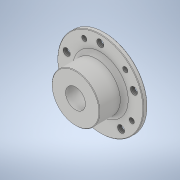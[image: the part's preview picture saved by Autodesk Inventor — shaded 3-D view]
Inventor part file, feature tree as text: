
AUTODESK INVENTOR PART (.ipt)
format: ipt  version: 2021 (Build 250183000, 183)  size: 223,232 bytes
history: native  units: in
note: dims shown in document units (in); Inventor stores cm internally (conversion verified against a paired STEP export)
features: thread x11, sketch x6, extrude x5, fillet x2, revolve x1, chamfer x1
ambient origin geometry x8: Origin, YZ Plane, XZ Plane, XY Plane, X Axis, Y Axis, Z Axis, Center Point
bodies: Solid1 (feature_tree)
feature tree (26):
  revolve  "Revolution1"  [1 undecoded]
  extrude  "Extrusion1"  Depth=0.26in
  extrude  "Extrusion2"  Depth=0.2in
  fillet  "Fillet1"  Radius=0.16in
  chamfer  "Chamfer1"  Distance=1.0in
  fillet  "Fillet2"  Radius=1.25in
  extrude  "Extrusion3"  Depth=0.26in TaperAngle=0.0deg
  thread  "Thread1"  [1 undecoded]
  thread  "Thread2"  [1 undecoded]
  thread  "Thread3"  [1 undecoded]
  thread  "Thread4"  [1 undecoded]
  thread  "Thread5"  [1 undecoded]
  thread  "Thread6"  [1 undecoded]
  extrude  "Extrusion4"  TaperAngle=45.0deg  [1 undecoded]
  extrude  "Extrusion5"  Depth=0.26in
  thread  "Thread7"  [1 undecoded]
  thread  "Thread8"  [1 undecoded]
  thread  "Thread9"  [1 undecoded]
  thread  "Thread10"  [1 undecoded]
  thread  "Thread11"  [1 undecoded]
  sketch  "Sketch1"  dims[d0=1.5in d1=1.56in]
  sketch  "Sketch2"  dims[d2=1.2in d3=0.26in]
  sketch  "Sketch3"  dims[d4=1.42in d5=0.2in d6=0.16in]
  sketch  "Sketch4"  dims[d7=0.52in]
  sketch  "Sketch5"  dims[d8=90.0deg]
  sketch  "Sketch6"  dims[d9=2.0in d10=1.0in d11=0.0in d12=1.25in d13=1.0in d14=0.0in d15=0.075in d16=0.03in d17=0.125in d18=45.0deg d19=0.25in d20=0.452in d21=0.48in d22=1.9685in d24=360.0deg d26=45.0deg d27=0.2in d28=0.2in d29=0.0in d30=0.435in d31=0.0in d32=0.435in d33=0.0in d34=0.435in d35=0.0in d36=0.435in d37=0.0in d38=0.435in d39=0.0in d40=0.435in d41=0.0in d42=1.0in d43=0.0in d44=0.325in d45=1.9685in d47=360.0deg d49=1.0in d50=0.0in d51=0.26in d52=0.0in d53=0.26in d54=0.0in d55=0.26in d56=0.0in d57=0.26in d58=0.0in d59=0.26in d60=0.0in]
note: 13 required parameter values undecoded (feature->parameter linkage not recoverable at this tier; creation-order binding heuristic only, values carry confidence <= 0.55)